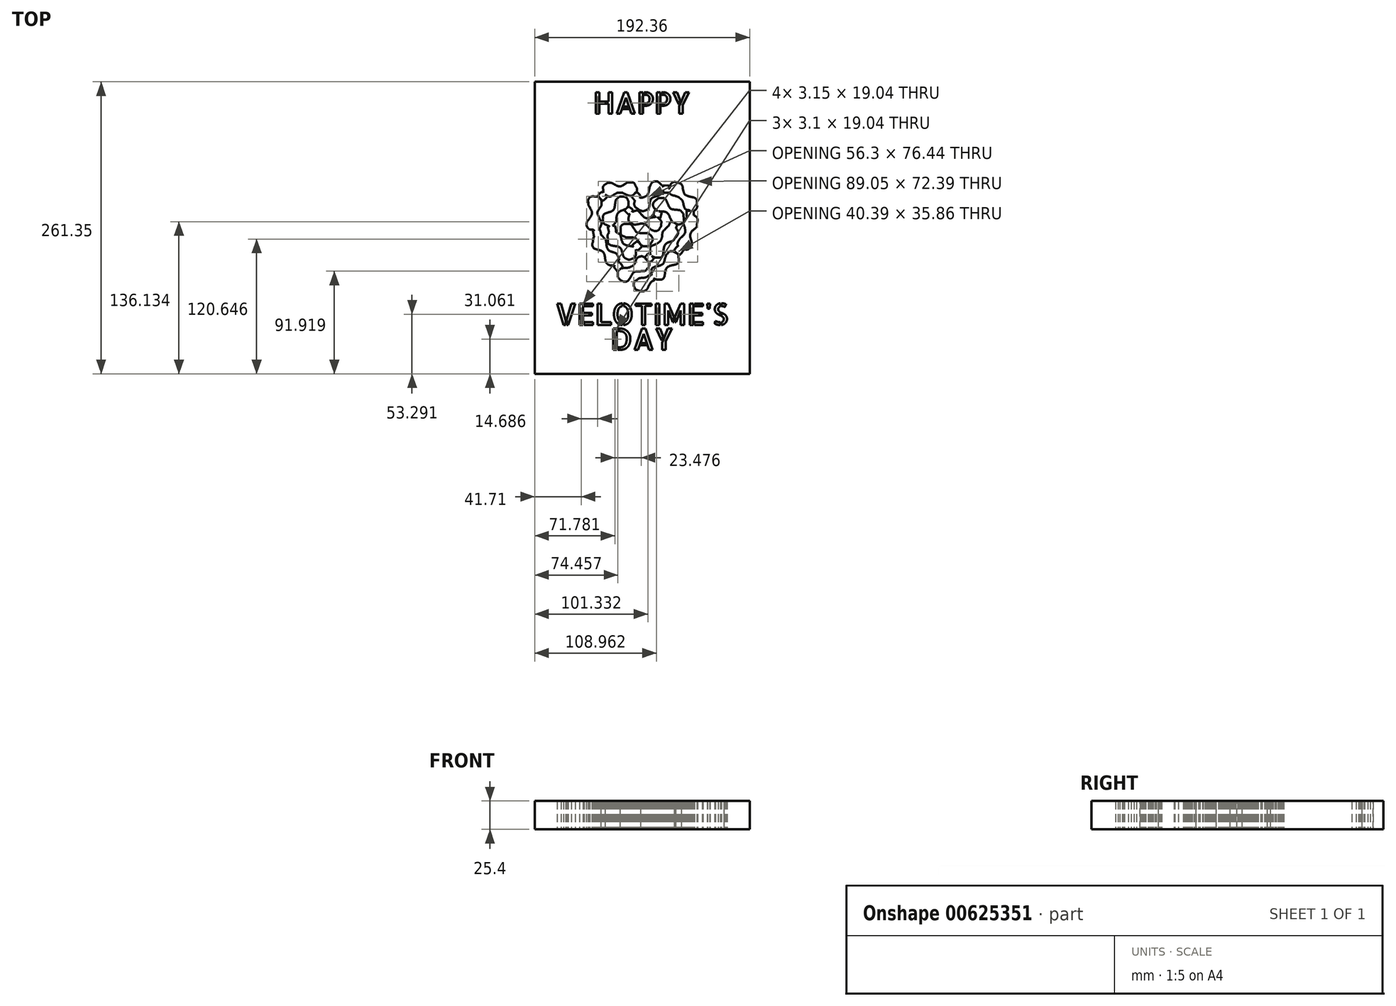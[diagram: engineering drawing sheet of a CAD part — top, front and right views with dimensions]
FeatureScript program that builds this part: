
annotation { "Feature Type Name" : "Feature", "Feature Type Description" : "" }
export const myFeature = defineFeature(function(context is Context, id is Id, definition is map)
    precondition{}
    {
        {
            var Q0;
            Q0=qCreatedBy(makeId("Top.planeOp"),FACE);
            var sketch = newSketch(context, id + "F0", { "sketchPlane" : qUnion([Q0])});
            skLineSegment(sketch, "E0", {"start": v(-21.62, 18.36) * mm, "end": v(-20.57, 16.33) * mm});
            skLineSegment(sketch, "E1", {"start": v(-20.57, 16.33) * mm, "end": v(-21.04, 14.87) * mm});
            skLineSegment(sketch, "E2", {"start": v(4.38, 19.7) * mm, "end": v(6.2, 21.31) * mm});
            skLineSegment(sketch, "E3", {"start": v(6.2, 21.31) * mm, "end": v(8.21, 19.14) * mm});
            skLineSegment(sketch, "E4", {"start": v(-25.38, 45.95) * mm, "end": v(-24.45, 45.98) * mm});
            skLineSegment(sketch, "E5", {"start": v(-24.45, 45.98) * mm, "end": v(-23.8, 43.65) * mm});
            skLineSegment(sketch, "E6", {"start": v(39.8, 56.85) * mm, "end": v(39.8, 59.27) * mm});
            skLineSegment(sketch, "E7", {"start": v(39.8, 59.27) * mm, "end": v(43.02, 59.2) * mm});
            skLineSegment(sketch, "E8", {"start": v(43.02, 59.2) * mm, "end": v(46.24, 59.12) * mm});
            skLineSegment(sketch, "E9", {"start": v(46.24, 59.12) * mm, "end": v(46.24, 56.66) * mm});
            skLineSegment(sketch, "E10", {"start": v(46.24, 56.66) * mm, "end": v(46.24, 54.2) * mm});
            skLineSegment(sketch, "E11", {"start": v(46.24, 54.2) * mm, "end": v(43.21, 54.11) * mm});
            skLineSegment(sketch, "E12", {"start": v(18.73, 78.7) * mm, "end": v(18.73, 82) * mm});
            skLineSegment(sketch, "E13", {"start": v(18.73, 82) * mm, "end": v(21.4, 81.92) * mm});
            skLineSegment(sketch, "E14", {"start": v(21.4, 81.92) * mm, "end": v(24.07, 81.84) * mm});
            skLineSegment(sketch, "E15", {"start": v(24.07, 81.84) * mm, "end": v(24.07, 78.7) * mm});
            skLineSegment(sketch, "E16", {"start": v(24.07, 78.7) * mm, "end": v(24.07, 75.54) * mm});
            skLineSegment(sketch, "E17", {"start": v(24.07, 75.54) * mm, "end": v(21.4, 75.47) * mm});
            skLineSegment(sketch, "E18", {"start": v(21.4, 75.47) * mm, "end": v(18.73, 75.39) * mm});
            skLineSegment(sketch, "E19", {"start": v(18.73, 75.39) * mm, "end": v(18.73, 78.7) * mm});
            skFitSpline(sketch, "E20", {"points": [v(-2.76, -12.29) * mm, v(-6.45, -10.34) * mm, v(-7.21, -5.2) * mm, v(-4.22, -2.42) * mm]});
            skFitSpline(sketch, "E21", {"points": [v(-4.22, -2.42) * mm, v(-3.3, -1.57) * mm, v(-1.94, -1.07) * mm, v(0.08, -0.85) * mm]});
            skFitSpline(sketch, "E22", {"points": [v(0.08, -0.85) * mm, v(2.4, -0.6) * mm, v(4.6, 0.26) * mm, v(5.86, 1.4) * mm]});
            skFitSpline(sketch, "E23", {"points": [v(5.86, 1.4) * mm, v(6.43, 1.9) * mm, v(7.02, 2.32) * mm, v(7.18, 2.32) * mm]});
            skFitSpline(sketch, "E24", {"points": [v(7.18, 2.32) * mm, v(7.56, 2.32) * mm, v(10.79, -2.16) * mm, v(10.79, -2.69) * mm]});
            skFitSpline(sketch, "E25", {"points": [v(10.79, -2.69) * mm, v(10.79, -2.91) * mm, v(10.42, -3.25) * mm, v(9.96, -3.44) * mm]});
            skFitSpline(sketch, "E26", {"points": [v(9.96, -3.44) * mm, v(8.68, -3.96) * mm, v(6.82, -6.24) * mm, v(5.54, -8.83) * mm]});
            skFitSpline(sketch, "E27", {"points": [v(5.54, -8.83) * mm, v(4.59, -10.77) * mm, v(4.17, -11.31) * mm, v(3.15, -11.96) * mm]});
            skFitSpline(sketch, "E28", {"points": [v(3.15, -11.96) * mm, v(2.1, -12.63) * mm, v(1.66, -12.74) * mm, v(0, -12.73) * mm]});
            skFitSpline(sketch, "E29", {"points": [v(0, -12.73) * mm, v(-1.22, -12.72) * mm, v(-2.25, -12.56) * mm, v(-2.76, -12.29) * mm]});
            skFitSpline(sketch, "E30", {"points": [v(-18.8, -3.07) * mm, v(-19.54, -2.69) * mm, v(-20.35, -1.94) * mm, v(-20.9, -1.13) * mm]});
            skFitSpline(sketch, "E31", {"points": [v(-20.9, -1.13) * mm, v(-21.68, 0.03) * mm, v(-21.79, 0.4) * mm, v(-21.79, 2.03) * mm]});
            skFitSpline(sketch, "E32", {"points": [v(-21.79, 2.03) * mm, v(-21.79, 4.3) * mm, v(-21.02, 5.93) * mm, v(-19.4, 7.07) * mm]});
            skFitSpline(sketch, "E33", {"points": [v(-19.4, 7.07) * mm, v(-18.4, 7.77) * mm, v(-17.97, 7.87) * mm, v(-15.04, 8.09) * mm]});
            skFitSpline(sketch, "E34", {"points": [v(-15.04, 8.09) * mm, v(-12.26, 8.3) * mm, v(-11.55, 8.45) * mm, v(-10.1, 9.17) * mm]});
            skFitSpline(sketch, "E35", {"points": [v(-10.1, 9.17) * mm, v(-8.3, 10.05) * mm, v(-6.97, 11.42) * mm, v(-5.96, 13.42) * mm]});
            skFitSpline(sketch, "E36", {"points": [v(-5.96, 13.42) * mm, v(-4, 17.32) * mm, v(0.8, 18.23) * mm, v(3.79, 15.28) * mm]});
            skFitSpline(sketch, "E37", {"points": [v(3.79, 15.28) * mm, v(6, 13.08) * mm, v(6.16, 9.55) * mm, v(4.16, 7.12) * mm]});
            skFitSpline(sketch, "E38", {"points": [v(4.16, 7.12) * mm, v(2.91, 5.6) * mm, v(1.99, 5.26) * mm, v(-1.4, 5.05) * mm]});
            skFitSpline(sketch, "E39", {"points": [v(-1.4, 5.05) * mm, v(-6.03, 4.77) * mm, v(-8.05, 3.6) * mm, v(-10.21, -0.01) * mm]});
            skFitSpline(sketch, "E40", {"points": [v(-10.21, -0.01) * mm, v(-10.75, -0.91) * mm, v(-11.4, -1.88) * mm, v(-11.63, -2.16) * mm]});
            skFitSpline(sketch, "E41", {"points": [v(-11.63, -2.16) * mm, v(-13.03, -3.79) * mm, v(-16.58, -4.24) * mm, v(-18.8, -3.07) * mm]});
            skFitSpline(sketch, "E42", {"points": [v(12.17, -2.03) * mm, v(9.83, -1.1) * mm, v(8.48, 0.99) * mm, v(8.48, 3.68) * mm]});
            skFitSpline(sketch, "E43", {"points": [v(8.48, 3.68) * mm, v(8.48, 6.78) * mm, v(9.84, 8.42) * mm, v(13.35, 9.53) * mm]});
            skFitSpline(sketch, "E44", {"points": [v(13.35, 9.53) * mm, v(17.5, 10.86) * mm, v(19.25, 12.5) * mm, v(20.39, 16.18) * mm]});
            skFitSpline(sketch, "E45", {"points": [v(20.39, 16.18) * mm, v(21.29, 19.07) * mm, v(21.73, 20) * mm, v(22.66, 20.9) * mm]});
            skFitSpline(sketch, "E46", {"points": [v(22.66, 20.9) * mm, v(24.55, 22.72) * mm, v(26.99, 23.05) * mm, v(29.42, 21.82) * mm]});
            skFitSpline(sketch, "E47", {"points": [v(29.42, 21.82) * mm, v(31.45, 20.8) * mm, v(32.48, 19.29) * mm, v(32.63, 17.13) * mm]});
            skFitSpline(sketch, "E48", {"points": [v(32.63, 17.13) * mm, v(32.89, 13.65) * mm, v(31.42, 11.73) * mm, v(27.66, 10.6) * mm]});
            skFitSpline(sketch, "E49", {"points": [v(27.66, 10.6) * mm, v(23.46, 9.36) * mm, v(21.28, 7.03) * mm, v(20.34, 2.74) * mm]});
            skFitSpline(sketch, "E50", {"points": [v(20.34, 2.74) * mm, v(19.65, -0.4) * mm, v(17.34, -2.35) * mm, v(14.36, -2.32) * mm]});
            skFitSpline(sketch, "E51", {"points": [v(14.36, -2.32) * mm, v(13.53, -2.31) * mm, v(12.54, -2.18) * mm, v(12.17, -2.03) * mm]});
            skFitSpline(sketch, "E52", {"points": [v(12.27, 1.29) * mm, v(10.96, 2.49) * mm, v(10.74, 3.96) * mm, v(11.66, 5.33) * mm]});
            skFitSpline(sketch, "E53", {"points": [v(11.66, 5.33) * mm, v(13.54, 8.1) * mm, v(17.5, 6.85) * mm, v(17.5, 3.47) * mm]});
            skFitSpline(sketch, "E54", {"points": [v(17.5, 3.47) * mm, v(17.5, 2.44) * mm, v(17.36, 2.15) * mm, v(16.47, 1.34) * mm]});
            skFitSpline(sketch, "E55", {"points": [v(16.47, 1.34) * mm, v(15.06, 0.05) * mm, v(13.65, 0.03) * mm, v(12.27, 1.29) * mm]});
            skFitSpline(sketch, "E56", {"points": [v(25.3, 13.77) * mm, v(24.73, 14.06) * mm, v(24.12, 14.7) * mm, v(23.82, 15.32) * mm]});
            skFitSpline(sketch, "E57", {"points": [v(23.82, 15.32) * mm, v(23.34, 16.27) * mm, v(23.33, 16.47) * mm, v(23.68, 17.48) * mm]});
            skFitSpline(sketch, "E58", {"points": [v(23.68, 17.48) * mm, v(24.38, 19.47) * mm, v(26.6, 20.4) * mm, v(28.3, 19.39) * mm]});
            skFitSpline(sketch, "E59", {"points": [v(28.3, 19.39) * mm, v(30.6, 18.03) * mm, v(30.45, 14.92) * mm, v(28.03, 13.67) * mm]});
            skFitSpline(sketch, "E60", {"points": [v(28.03, 13.67) * mm, v(27, 13.14) * mm, v(26.45, 13.16) * mm, v(25.3, 13.77) * mm]});
            skFitSpline(sketch, "E61", {"points": [v(-23.93, 7.17) * mm, v(-24.7, 8.22) * mm, v(-25.22, 9.16) * mm, v(-25.11, 9.35) * mm]});
            skFitSpline(sketch, "E62", {"points": [v(-25.11, 9.35) * mm, v(-24.79, 9.93) * mm, v(-21.01, 13) * mm, v(-20.62, 13) * mm]});
            skFitSpline(sketch, "E63", {"points": [v(-20.62, 13) * mm, v(-20.23, 13) * mm, v(-17.68, 9.7) * mm, v(-17.68, 9.2) * mm]});
            skFitSpline(sketch, "E64", {"points": [v(-17.68, 9.2) * mm, v(-17.68, 8.9) * mm, v(-22.02, 5.33) * mm, v(-22.37, 5.33) * mm]});
            skFitSpline(sketch, "E65", {"points": [v(-22.37, 5.33) * mm, v(-22.47, 5.33) * mm, v(-23.17, 6.16) * mm, v(-23.93, 7.17) * mm]});
            skFitSpline(sketch, "E66", {"points": [v(-29.45, 10.7) * mm, v(-30.6, 11.19) * mm, v(-31.82, 12.3) * mm, v(-32.36, 13.33) * mm]});
            skFitSpline(sketch, "E67", {"points": [v(-32.36, 13.33) * mm, v(-32.57, 13.74) * mm, v(-32.92, 15.08) * mm, v(-33.14, 16.3) * mm]});
            skFitSpline(sketch, "E68", {"points": [v(-33.14, 16.3) * mm, v(-33.88, 20.58) * mm, v(-35.68, 22.88) * mm, v(-39.36, 24.26) * mm]});
            skFitSpline(sketch, "E69", {"points": [v(-39.36, 24.26) * mm, v(-42.91, 25.58) * mm, v(-44.63, 28.37) * mm, v(-43.93, 31.64) * mm]});
            skFitSpline(sketch, "E70", {"points": [v(-43.93, 31.64) * mm, v(-43.01, 35.9) * mm, v(-37.5, 37.72) * mm, v(-34.22, 34.84) * mm]});
            skFitSpline(sketch, "E71", {"points": [v(-34.22, 34.84) * mm, v(-32.92, 33.7) * mm, v(-32.52, 32.84) * mm, v(-32.06, 30.2) * mm]});
            skFitSpline(sketch, "E72", {"points": [v(-32.06, 30.2) * mm, v(-31.33, 25.98) * mm, v(-29.5, 23.59) * mm, v(-25.96, 22.17) * mm]});
            skFitSpline(sketch, "E73", {"points": [v(-25.96, 22.17) * mm, v(-23.35, 21.12) * mm, v(-22.79, 20.63) * mm, v(-21.62, 18.36) * mm]});
            skFitSpline(sketch, "E74", {"points": [v(-21.04, 14.87) * mm, v(-21.95, 11.97) * mm, v(-24.19, 10.25) * mm, v(-27, 10.27) * mm]});
            skFitSpline(sketch, "E75", {"points": [v(-27, 10.27) * mm, v(-27.82, 10.27) * mm, v(-28.92, 10.46) * mm, v(-29.45, 10.7) * mm]});
            skFitSpline(sketch, "E76", {"points": [v(4.36, 15.2) * mm, v(3.45, 16.27) * mm, v(2.68, 17.36) * mm, v(2.63, 17.62) * mm]});
            skFitSpline(sketch, "E77", {"points": [v(2.63, 17.62) * mm, v(2.58, 17.93) * mm, v(3.2, 18.68) * mm, v(4.38, 19.7) * mm]});
            skFitSpline(sketch, "E78", {"points": [v(8.21, 19.14) * mm, v(9.32, 17.94) * mm, v(10.23, 16.82) * mm, v(10.23, 16.64) * mm]});
            skFitSpline(sketch, "E79", {"points": [v(10.23, 16.64) * mm, v(10.25, 16.19) * mm, v(6.95, 13.27) * mm, v(6.43, 13.27) * mm]});
            skFitSpline(sketch, "E80", {"points": [v(6.43, 13.27) * mm, v(6.2, 13.27) * mm, v(5.26, 14.15) * mm, v(4.36, 15.2) * mm]});
            skFitSpline(sketch, "E81", {"points": [v(-14.15, 16.27) * mm, v(-15.65, 17.07) * mm, v(-16.73, 18.5) * mm, v(-17.4, 20.56) * mm]});
            skFitSpline(sketch, "E82", {"points": [v(-17.4, 20.56) * mm, v(-18.8, 24.84) * mm, v(-20.89, 26.8) * mm, v(-25.07, 27.77) * mm]});
            skFitSpline(sketch, "E83", {"points": [v(-25.07, 27.77) * mm, v(-28.83, 28.64) * mm, v(-30.6, 30.58) * mm, v(-30.58, 33.8) * mm]});
            skFitSpline(sketch, "E84", {"points": [v(-30.58, 33.8) * mm, v(-30.56, 38.4) * mm, v(-26, 41.19) * mm, v(-21.9, 39.14) * mm]});
            skFitSpline(sketch, "E85", {"points": [v(-21.9, 39.14) * mm, v(-20.18, 38.28) * mm, v(-19.52, 37.4) * mm, v(-18.8, 35) * mm]});
            skFitSpline(sketch, "E86", {"points": [v(-18.8, 35) * mm, v(-17.57, 30.83) * mm, v(-15.25, 28.7) * mm, v(-10.83, 27.66) * mm]});
            skFitSpline(sketch, "E87", {"points": [v(-10.83, 27.66) * mm, v(-7.23, 26.81) * mm, v(-5.64, 24.96) * mm, v(-5.64, 21.61) * mm]});
            skFitSpline(sketch, "E88", {"points": [v(-5.64, 21.61) * mm, v(-5.64, 19.17) * mm, v(-7.02, 17.09) * mm, v(-9.25, 16.16) * mm]});
            skFitSpline(sketch, "E89", {"points": [v(-9.25, 16.16) * mm, v(-10.64, 15.57) * mm, v(-12.93, 15.63) * mm, v(-14.15, 16.27) * mm]});
            skFitSpline(sketch, "E90", {"points": [v(10.38, 17.83) * mm, v(8.2, 18.98) * mm, v(7.23, 20.65) * mm, v(7.23, 23.26) * mm]});
            skFitSpline(sketch, "E91", {"points": [v(7.23, 23.26) * mm, v(7.23, 26.33) * mm, v(8.01, 27.38) * mm, v(11.48, 29) * mm]});
            skFitSpline(sketch, "E92", {"points": [v(11.48, 29) * mm, v(12.84, 29.63) * mm, v(14.41, 30.55) * mm, v(14.97, 31.04) * mm]});
            skFitSpline(sketch, "E93", {"points": [v(14.97, 31.04) * mm, v(16.33, 32.24) * mm, v(17.55, 34.84) * mm, v(17.93, 37.36) * mm]});
            skFitSpline(sketch, "E94", {"points": [v(17.93, 37.36) * mm, v(18.3, 39.8) * mm, v(18.96, 41.2) * mm, v(20.16, 42.1) * mm]});
            skFitSpline(sketch, "E95", {"points": [v(20.16, 42.1) * mm, v(25.43, 46) * mm, v(32.15, 40.5) * mm, v(29.24, 34.67) * mm]});
            skFitSpline(sketch, "E96", {"points": [v(29.24, 34.67) * mm, v(28.42, 33.02) * mm, v(27.73, 32.47) * mm, v(25.23, 31.47) * mm]});
            skFitSpline(sketch, "E97", {"points": [v(25.23, 31.47) * mm, v(21.67, 30.04) * mm, v(19.87, 27.65) * mm, v(19.12, 23.38) * mm]});
            skFitSpline(sketch, "E98", {"points": [v(19.12, 23.38) * mm, v(18.38, 19.12) * mm, v(16.61, 17.36) * mm, v(13.1, 17.38) * mm]});
            skFitSpline(sketch, "E99", {"points": [v(13.1, 17.38) * mm, v(11.92, 17.4) * mm, v(10.9, 17.56) * mm, v(10.38, 17.83) * mm]});
            skFitSpline(sketch, "E100", {"points": [v(10.85, 20.91) * mm, v(9.86, 21.9) * mm, v(9.58, 23.13) * mm, v(10.08, 24.32) * mm]});
            skFitSpline(sketch, "E101", {"points": [v(10.08, 24.32) * mm, v(11.5, 27.74) * mm, v(16.26, 26.7) * mm, v(16.26, 22.97) * mm]});
            skFitSpline(sketch, "E102", {"points": [v(16.26, 22.97) * mm, v(16.26, 22.2) * mm, v(16.05, 21.76) * mm, v(15.33, 21.04) * mm]});
            skFitSpline(sketch, "E103", {"points": [v(15.33, 21.04) * mm, v(14.52, 20.23) * mm, v(14.23, 20.1) * mm, v(13.03, 20.1) * mm]});
            skFitSpline(sketch, "E104", {"points": [v(13.03, 20.1) * mm, v(11.87, 20.1) * mm, v(11.53, 20.24) * mm, v(10.85, 20.91) * mm]});
            skFitSpline(sketch, "E105", {"points": [v(22.84, 34.38) * mm, v(20.44, 35.33) * mm, v(20.07, 38.4) * mm, v(22.15, 40.05) * mm]});
            skFitSpline(sketch, "E106", {"points": [v(22.15, 40.05) * mm, v(24.11, 41.59) * mm, v(27.22, 39.99) * mm, v(27.21, 37.44) * mm]});
            skFitSpline(sketch, "E107", {"points": [v(27.21, 37.44) * mm, v(27.21, 36.32) * mm, v(26.25, 34.92) * mm, v(25.16, 34.47) * mm]});
            skFitSpline(sketch, "E108", {"points": [v(25.16, 34.47) * mm, v(24.08, 34.01) * mm, v(23.78, 34) * mm, v(22.84, 34.38) * mm]});
            skFitSpline(sketch, "E109", {"points": [v(30.92, 21.36) * mm, v(29.78, 22.35) * mm, v(28.86, 23.34) * mm, v(28.86, 23.56) * mm]});
            skFitSpline(sketch, "E110", {"points": [v(28.86, 23.56) * mm, v(28.86, 24.02) * mm, v(31.53, 27.5) * mm, v(31.9, 27.5) * mm]});
            skFitSpline(sketch, "E111", {"points": [v(31.9, 27.5) * mm, v(32.2, 27.5) * mm, v(36.52, 23.71) * mm, v(36.52, 23.44) * mm]});
            skFitSpline(sketch, "E112", {"points": [v(36.52, 23.44) * mm, v(36.52, 23.12) * mm, v(33.5, 19.56) * mm, v(33.23, 19.56) * mm]});
            skFitSpline(sketch, "E113", {"points": [v(33.23, 19.56) * mm, v(33.1, 19.56) * mm, v(32.05, 20.37) * mm, v(30.92, 21.36) * mm]});
            skFitSpline(sketch, "E114", {"points": [v(-6.7, 25.83) * mm, v(-7.77, 27.01) * mm, v(-8.65, 28.12) * mm, v(-8.65, 28.28) * mm]});
            skFitSpline(sketch, "E115", {"points": [v(-8.65, 28.28) * mm, v(-8.65, 28.62) * mm, v(-4.79, 31.6) * mm, v(-4.35, 31.6) * mm]});
            skFitSpline(sketch, "E116", {"points": [v(-4.35, 31.6) * mm, v(-3.98, 31.6) * mm, v(-0.36, 27.3) * mm, v(-0.48, 26.98) * mm]});
            skFitSpline(sketch, "E117", {"points": [v(-0.48, 26.98) * mm, v(-0.6, 26.65) * mm, v(-4.25, 23.67) * mm, v(-4.53, 23.67) * mm]});
            skFitSpline(sketch, "E118", {"points": [v(-4.53, 23.67) * mm, v(-4.66, 23.67) * mm, v(-5.63, 24.64) * mm, v(-6.7, 25.83) * mm]});
            skFitSpline(sketch, "E119", {"points": [v(36.26, 24.8) * mm, v(33.3, 25.98) * mm, v(31.64, 29.76) * mm, v(32.84, 32.63) * mm]});
            skFitSpline(sketch, "E120", {"points": [v(32.84, 32.63) * mm, v(33.07, 33.18) * mm, v(34, 34.4) * mm, v(34.9, 35.34) * mm]});
            skFitSpline(sketch, "E121", {"points": [v(34.9, 35.34) * mm, v(37.9, 38.48) * mm, v(38.65, 41.49) * mm, v(37.52, 45.9) * mm]});
            skFitSpline(sketch, "E122", {"points": [v(37.52, 45.9) * mm, v(36.8, 48.74) * mm, v(37.25, 50.43) * mm, v(39.22, 52.2) * mm]});
            skFitSpline(sketch, "E123", {"points": [v(39.22, 52.2) * mm, v(43.12, 55.73) * mm, v(49.11, 52.97) * mm, v(49.11, 47.66) * mm]});
            skFitSpline(sketch, "E124", {"points": [v(49.11, 47.66) * mm, v(49.11, 45.7) * mm, v(48.52, 44.5) * mm, v(46.62, 42.7) * mm]});
            skFitSpline(sketch, "E125", {"points": [v(46.62, 42.7) * mm, v(43.82, 40.03) * mm, v(42.98, 36.65) * mm, v(44.06, 32.37) * mm]});
            skFitSpline(sketch, "E126", {"points": [v(44.06, 32.37) * mm, v(44.66, 29.98) * mm, v(44.44, 28.42) * mm, v(43.28, 26.9) * mm]});
            skFitSpline(sketch, "E127", {"points": [v(43.28, 26.9) * mm, v(42.07, 25.32) * mm, v(40.4, 24.49) * mm, v(38.46, 24.5) * mm]});
            skFitSpline(sketch, "E128", {"points": [v(38.46, 24.5) * mm, v(37.62, 24.52) * mm, v(36.63, 24.65) * mm, v(36.26, 24.8) * mm]});
            skFitSpline(sketch, "E129", {"points": [v(-0.01, 28.1) * mm, v(-0.6, 28.45) * mm, v(-1.5, 29.29) * mm, v(-2, 29.97) * mm]});
            skFitSpline(sketch, "E130", {"points": [v(-2, 29.97) * mm, v(-4.52, 33.41) * mm, v(-6.2, 34.76) * mm, v(-8.65, 35.32) * mm]});
            skFitSpline(sketch, "E131", {"points": [v(-8.65, 35.32) * mm, v(-9.17, 35.43) * mm, v(-10.71, 35.5) * mm, v(-12.07, 35.48) * mm]});
            skFitSpline(sketch, "E132", {"points": [v(-12.07, 35.48) * mm, v(-14.29, 35.43) * mm, v(-14.7, 35.5) * mm, v(-16.04, 36.18) * mm]});
            skFitSpline(sketch, "E133", {"points": [v(-16.04, 36.18) * mm, v(-18.14, 37.25) * mm, v(-19.2, 38.97) * mm, v(-19.17, 41.3) * mm]});
            skFitSpline(sketch, "E134", {"points": [v(-19.17, 41.3) * mm, v(-19.15, 44.86) * mm, v(-16.71, 47.3) * mm, v(-13.16, 47.31) * mm]});
            skFitSpline(sketch, "E135", {"points": [v(-13.16, 47.31) * mm, v(-10.75, 47.33) * mm, v(-9.53, 46.6) * mm, v(-7.85, 44.1) * mm]});
            skFitSpline(sketch, "E136", {"points": [v(-7.85, 44.1) * mm, v(-5.3, 40.3) * mm, v(-3.82, 39.54) * mm, v(1.35, 39.28) * mm]});
            skFitSpline(sketch, "E137", {"points": [v(1.35, 39.28) * mm, v(5.09, 39.1) * mm, v(6, 38.83) * mm, v(7.13, 37.59) * mm]});
            skFitSpline(sketch, "E138", {"points": [v(7.13, 37.59) * mm, v(8.9, 35.63) * mm, v(9.25, 32.63) * mm, v(7.95, 30.41) * mm]});
            skFitSpline(sketch, "E139", {"points": [v(7.95, 30.41) * mm, v(6.82, 28.49) * mm, v(5.4, 27.66) * mm, v(3.01, 27.56) * mm]});
            skFitSpline(sketch, "E140", {"points": [v(3.01, 27.56) * mm, v(1.4, 27.5) * mm, v(0.9, 27.58) * mm, v(-0.01, 28.1) * mm]});
            skFitSpline(sketch, "E141", {"points": [v(-42.96, 35.92) * mm, v(-43.03, 36.03) * mm, v(-43.3, 37.21) * mm, v(-43.57, 38.55) * mm]});
            skFitSpline(sketch, "E142", {"points": [v(-43.57, 38.55) * mm, v(-43.94, 40.43) * mm, v(-43.97, 41.01) * mm, v(-43.71, 41.17) * mm]});
            skFitSpline(sketch, "E143", {"points": [v(-43.71, 41.17) * mm, v(-43.14, 41.53) * mm, v(-38.24, 42.68) * mm, v(-38.06, 42.5) * mm]});
            skFitSpline(sketch, "E144", {"points": [v(-38.06, 42.5) * mm, v(-37.83, 42.27) * mm, v(-36.85, 38.44) * mm, v(-36.85, 37.74) * mm]});
            skFitSpline(sketch, "E145", {"points": [v(-36.85, 37.74) * mm, v(-36.84, 37.24) * mm, v(-37.2, 37.07) * mm, v(-39.65, 36.44) * mm]});
            skFitSpline(sketch, "E146", {"points": [v(-39.65, 36.44) * mm, v(-42.75, 35.63) * mm, v(-42.78, 35.63) * mm, v(-42.96, 35.92) * mm]});
            skFitSpline(sketch, "E147", {"points": [v(-29.26, 39.47) * mm, v(-29.52, 39.9) * mm, v(-30.55, 43.84) * mm, v(-30.55, 44.4) * mm]});
            skFitSpline(sketch, "E148", {"points": [v(-30.55, 44.4) * mm, v(-30.55, 44.9) * mm, v(-30.25, 45.05) * mm, v(-28.42, 45.46) * mm]});
            skFitSpline(sketch, "E149", {"points": [v(-28.42, 45.46) * mm, v(-27.26, 45.72) * mm, v(-25.89, 45.94) * mm, v(-25.38, 45.95) * mm]});
            skFitSpline(sketch, "E150", {"points": [v(-23.8, 43.65) * mm, v(-23.45, 42.37) * mm, v(-23.21, 41.19) * mm, v(-23.27, 41.02) * mm]});
            skFitSpline(sketch, "E151", {"points": [v(-23.27, 41.02) * mm, v(-23.33, 40.86) * mm, v(-24.47, 40.45) * mm, v(-25.8, 40.12) * mm]});
            skFitSpline(sketch, "E152", {"points": [v(-25.8, 40.12) * mm, v(-27.13, 39.8) * mm, v(-28.42, 39.46) * mm, v(-28.68, 39.39) * mm]});
            skFitSpline(sketch, "E153", {"points": [v(-28.68, 39.39) * mm, v(-28.93, 39.31) * mm, v(-29.19, 39.35) * mm, v(-29.26, 39.47) * mm]});
            skFitSpline(sketch, "E154", {"points": [v(9.2, 41.78) * mm, v(8.63, 41.94) * mm, v(7.49, 42.83) * mm, v(6.22, 44.1) * mm]});
            skFitSpline(sketch, "E155", {"points": [v(6.22, 44.1) * mm, v(4.14, 46.2) * mm, v(2.21, 47.36) * mm, v(0.27, 47.67) * mm]});
            skFitSpline(sketch, "E156", {"points": [v(0.27, 47.67) * mm, v(-0.26, 47.76) * mm, v(-1.81, 47.61) * mm, v(-3.17, 47.35) * mm]});
            skFitSpline(sketch, "E157", {"points": [v(-3.17, 47.35) * mm, v(-6.08, 46.78) * mm, v(-7.38, 46.9) * mm, v(-9.05, 47.88) * mm]});
            skFitSpline(sketch, "E158", {"points": [v(-9.05, 47.88) * mm, v(-11.24, 49.16) * mm, v(-12.35, 52.02) * mm, v(-11.66, 54.6) * mm]});
            skFitSpline(sketch, "E159", {"points": [v(-11.66, 54.6) * mm, v(-11.23, 56.2) * mm, v(-9.22, 58.25) * mm, v(-7.69, 58.68) * mm]});
            skFitSpline(sketch, "E160", {"points": [v(-7.69, 58.68) * mm, v(-4.98, 59.42) * mm, v(-3.3, 58.87) * mm, v(-1.03, 56.49) * mm]});
            skFitSpline(sketch, "E161", {"points": [v(-1.03, 56.49) * mm, v(1.85, 53.45) * mm, v(4.52, 52.4) * mm, v(7.8, 52.97) * mm]});
            skFitSpline(sketch, "E162", {"points": [v(7.8, 52.97) * mm, v(12.18, 53.74) * mm, v(13.33, 53.6) * mm, v(15.07, 52.07) * mm]});
            skFitSpline(sketch, "E163", {"points": [v(15.07, 52.07) * mm, v(16.62, 50.71) * mm, v(17.16, 49.36) * mm, v(17.04, 47.18) * mm]});
            skFitSpline(sketch, "E164", {"points": [v(17.04, 47.18) * mm, v(16.95, 45.66) * mm, v(16.78, 45.1) * mm, v(16.12, 44.14) * mm]});
            skFitSpline(sketch, "E165", {"points": [v(16.12, 44.14) * mm, v(14.63, 42) * mm, v(11.79, 41.03) * mm, v(9.2, 41.78) * mm]});
            skFitSpline(sketch, "E166", {"points": [v(-44.14, 42.26) * mm, v(-48.28, 43.3) * mm, v(-49.83, 47.83) * mm, v(-47.43, 51.86) * mm]});
            skFitSpline(sketch, "E167", {"points": [v(-47.43, 51.86) * mm, v(-45.13, 55.72) * mm, v(-45.01, 58.39) * mm, v(-46.97, 62.27) * mm]});
            skFitSpline(sketch, "E168", {"points": [v(-46.97, 62.27) * mm, v(-47.95, 64.2) * mm, v(-48.15, 64.85) * mm, v(-48.14, 66.12) * mm]});
            skFitSpline(sketch, "E169", {"points": [v(-48.14, 66.12) * mm, v(-48.11, 69.54) * mm, v(-45.68, 71.92) * mm, v(-42.18, 71.96) * mm]});
            skFitSpline(sketch, "E170", {"points": [v(-42.18, 71.96) * mm, v(-40.12, 71.98) * mm, v(-38.46, 71.13) * mm, v(-37.27, 69.43) * mm]});
            skFitSpline(sketch, "E171", {"points": [v(-37.27, 69.43) * mm, v(-36.51, 68.35) * mm, v(-36.43, 68.04) * mm, v(-36.43, 66.12) * mm]});
            skFitSpline(sketch, "E172", {"points": [v(-36.43, 66.12) * mm, v(-36.43, 64.15) * mm, v(-36.5, 63.89) * mm, v(-37.46, 62.33) * mm]});
            skFitSpline(sketch, "E173", {"points": [v(-37.46, 62.33) * mm, v(-39.83, 58.5) * mm, v(-39.92, 56.52) * mm, v(-37.94, 51.98) * mm]});
            skFitSpline(sketch, "E174", {"points": [v(-37.94, 51.98) * mm, v(-36.5, 48.65) * mm, v(-36.32, 47.6) * mm, v(-36.97, 46.05) * mm]});
            skFitSpline(sketch, "E175", {"points": [v(-36.97, 46.05) * mm, v(-38.14, 43.23) * mm, v(-41.32, 41.56) * mm, v(-44.14, 42.26) * mm]});
            skFitSpline(sketch, "E176", {"points": [v(26.4, 43.27) * mm, v(25.11, 43.8) * mm, v(23.96, 44.34) * mm, v(23.84, 44.46) * mm]});
            skFitSpline(sketch, "E177", {"points": [v(23.84, 44.46) * mm, v(23.59, 44.7) * mm, v(25.5, 49.4) * mm, v(25.86, 49.4) * mm]});
            skFitSpline(sketch, "E178", {"points": [v(25.86, 49.4) * mm, v(26.3, 49.4) * mm, v(31.32, 46.96) * mm, v(31.32, 46.75) * mm]});
            skFitSpline(sketch, "E179", {"points": [v(31.32, 46.75) * mm, v(31.32, 46.63) * mm, v(30.94, 45.57) * mm, v(30.47, 44.4) * mm]});
            skFitSpline(sketch, "E180", {"points": [v(30.47, 44.4) * mm, v(29.89, 42.95) * mm, v(29.48, 42.29) * mm, v(29.17, 42.3) * mm]});
            skFitSpline(sketch, "E181", {"points": [v(29.17, 42.3) * mm, v(28.92, 42.3) * mm, v(27.67, 42.74) * mm, v(26.4, 43.27) * mm]});
            skFitSpline(sketch, "E182", {"points": [v(-31.5, 46.36) * mm, v(-33.7, 47.38) * mm, v(-34.93, 49.4) * mm, v(-34.93, 52) * mm]});
            skFitSpline(sketch, "E183", {"points": [v(-34.93, 52) * mm, v(-34.93, 54.72) * mm, v(-33.62, 56.43) * mm, v(-30.65, 57.62) * mm]});
            skFitSpline(sketch, "E184", {"points": [v(-30.65, 57.62) * mm, v(-26.5, 59.27) * mm, v(-24.92, 61.26) * mm, v(-24.1, 65.85) * mm]});
            skFitSpline(sketch, "E185", {"points": [v(-24.1, 65.85) * mm, v(-23.65, 68.47) * mm, v(-23.22, 69.32) * mm, v(-21.75, 70.59) * mm]});
            skFitSpline(sketch, "E186", {"points": [v(-21.75, 70.59) * mm, v(-20.45, 71.7) * mm, v(-19.42, 71.97) * mm, v(-17.25, 71.79) * mm]});
            skFitSpline(sketch, "E187", {"points": [v(-17.25, 71.79) * mm, v(-15.35, 71.63) * mm, v(-13.74, 70.56) * mm, v(-12.82, 68.84) * mm]});
            skFitSpline(sketch, "E188", {"points": [v(-12.82, 68.84) * mm, v(-12.27, 67.8) * mm, v(-12.18, 67.3) * mm, v(-12.26, 65.64) * mm]});
            skFitSpline(sketch, "E189", {"points": [v(-12.26, 65.64) * mm, v(-12.34, 63.98) * mm, v(-12.48, 63.5) * mm, v(-13.17, 62.52) * mm]});
            skFitSpline(sketch, "E190", {"points": [v(-13.17, 62.52) * mm, v(-14, 61.36) * mm, v(-14.45, 61.06) * mm, v(-17.73, 59.54) * mm]});
            skFitSpline(sketch, "E191", {"points": [v(-17.73, 59.54) * mm, v(-20.84, 58.1) * mm, v(-22.54, 55.58) * mm, v(-23.01, 51.73) * mm]});
            skFitSpline(sketch, "E192", {"points": [v(-23.01, 51.73) * mm, v(-23.24, 49.85) * mm, v(-23.86, 48.49) * mm, v(-24.98, 47.43) * mm]});
            skFitSpline(sketch, "E193", {"points": [v(-24.98, 47.43) * mm, v(-26.65, 45.84) * mm, v(-29.4, 45.4) * mm, v(-31.5, 46.36) * mm]});
            skFitSpline(sketch, "E194", {"points": [v(29.03, 48.43) * mm, v(27.46, 49) * mm, v(26.48, 50.08) * mm, v(25.13, 52.76) * mm]});
            skFitSpline(sketch, "E195", {"points": [v(25.13, 52.76) * mm, v(23.18, 56.62) * mm, v(21.14, 58.12) * mm, v(17.22, 58.57) * mm]});
            skFitSpline(sketch, "E196", {"points": [v(17.22, 58.57) * mm, v(14.9, 58.83) * mm, v(13.9, 59.2) * mm, v(12.78, 60.17) * mm]});
            skFitSpline(sketch, "E197", {"points": [v(12.78, 60.17) * mm, v(10.12, 62.5) * mm, v(10.1, 66.5) * mm, v(12.75, 69.03) * mm]});
            skFitSpline(sketch, "E198", {"points": [v(12.75, 69.03) * mm, v(13.94, 70.16) * mm, v(14.84, 70.48) * mm, v(16.84, 70.48) * mm]});
            skFitSpline(sketch, "E199", {"points": [v(16.84, 70.48) * mm, v(19.73, 70.48) * mm, v(21.07, 69.46) * mm, v(22.7, 66) * mm]});
            skFitSpline(sketch, "E200", {"points": [v(22.7, 66) * mm, v(24.46, 62.26) * mm, v(26.7, 60.66) * mm, v(31.03, 60.07) * mm]});
            skFitSpline(sketch, "E201", {"points": [v(31.03, 60.07) * mm, v(33.72, 59.71) * mm, v(34.48, 59.38) * mm, v(35.68, 58) * mm]});
            skFitSpline(sketch, "E202", {"points": [v(35.68, 58) * mm, v(36.82, 56.7) * mm, v(37.07, 56) * mm, v(37.06, 54.1) * mm]});
            skFitSpline(sketch, "E203", {"points": [v(37.06, 54.1) * mm, v(37.05, 49.75) * mm, v(33.12, 46.98) * mm, v(29.03, 48.43) * mm]});
            skFitSpline(sketch, "E204", {"points": [v(13.15, 53.51) * mm, v(11.81, 53.94) * mm, v(10.6, 54.42) * mm, v(10.44, 54.57) * mm]});
            skFitSpline(sketch, "E205", {"points": [v(10.44, 54.57) * mm, v(10.13, 54.88) * mm, v(11.22, 59.15) * mm, v(11.67, 59.43) * mm]});
            skFitSpline(sketch, "E206", {"points": [v(11.67, 59.43) * mm, v(12.03, 59.65) * mm, v(17.13, 57.81) * mm, v(17.3, 57.4) * mm]});
            skFitSpline(sketch, "E207", {"points": [v(17.3, 57.4) * mm, v(17.37, 57.2) * mm, v(17.24, 56.4) * mm, v(17, 55.62) * mm]});
            skFitSpline(sketch, "E208", {"points": [v(17, 55.62) * mm, v(16.77, 54.83) * mm, v(16.5, 53.85) * mm, v(16.42, 53.44) * mm]});
            skFitSpline(sketch, "E209", {"points": [v(16.42, 53.44) * mm, v(16.22, 52.53) * mm, v(16.21, 52.53) * mm, v(13.15, 53.51) * mm]});
            skFitSpline(sketch, "E210", {"points": [v(40, 54.23) * mm, v(39.9, 54.33) * mm, v(39.8, 55.51) * mm, v(39.8, 56.85) * mm]});
            skFitSpline(sketch, "E211", {"points": [v(43.21, 54.11) * mm, v(41.55, 54.07) * mm, v(40.1, 54.12) * mm, v(40, 54.23) * mm]});
            skFitSpline(sketch, "E212", {"points": [v(-13.92, 57.55) * mm, v(-14.79, 58.42) * mm, v(-15.5, 59.28) * mm, v(-15.5, 59.45) * mm]});
            skFitSpline(sketch, "E213", {"points": [v(-15.5, 59.45) * mm, v(-15.5, 59.81) * mm, v(-12.33, 62.68) * mm, v(-11.93, 62.68) * mm]});
            skFitSpline(sketch, "E214", {"points": [v(-11.93, 62.68) * mm, v(-11.51, 62.68) * mm, v(-8.37, 59.8) * mm, v(-8.4, 59.45) * mm]});
            skFitSpline(sketch, "E215", {"points": [v(-8.4, 59.45) * mm, v(-8.43, 59.09) * mm, v(-11.78, 55.97) * mm, v(-12.14, 55.97) * mm]});
            skFitSpline(sketch, "E216", {"points": [v(-12.14, 55.97) * mm, v(-12.26, 55.97) * mm, v(-13.06, 56.68) * mm, v(-13.92, 57.55) * mm]});
            skFitSpline(sketch, "E217", {"points": [v(-0.3, 59.1) * mm, v(-0.45, 59.16) * mm, v(-0.91, 59.28) * mm, v(-1.33, 59.38) * mm]});
            skFitSpline(sketch, "E218", {"points": [v(-1.33, 59.38) * mm, v(-1.75, 59.47) * mm, v(-2.6, 60) * mm, v(-3.22, 60.56) * mm]});
            skFitSpline(sketch, "E219", {"points": [v(-3.22, 60.56) * mm, v(-6.85, 63.84) * mm, v(-5.65, 69.48) * mm, v(-1.03, 70.85) * mm]});
            skFitSpline(sketch, "E220", {"points": [v(-1.03, 70.85) * mm, v(3.28, 72.13) * mm, v(5.3, 74.33) * mm, v(6.37, 78.92) * mm]});
            skFitSpline(sketch, "E221", {"points": [v(6.37, 78.92) * mm, v(6.65, 80.16) * mm, v(7.2, 81.64) * mm, v(7.59, 82.22) * mm]});
            skFitSpline(sketch, "E222", {"points": [v(7.59, 82.22) * mm, v(9.38, 84.93) * mm, v(13.93, 85.3) * mm, v(16.5, 82.97) * mm]});
            skFitSpline(sketch, "E223", {"points": [v(16.5, 82.97) * mm, v(18.41, 81.23) * mm, v(18.9, 77.91) * mm, v(17.58, 75.66) * mm]});
            skFitSpline(sketch, "E224", {"points": [v(17.58, 75.66) * mm, v(16.7, 74.16) * mm, v(15.44, 73.27) * mm, v(12.74, 72.24) * mm]});
            skFitSpline(sketch, "E225", {"points": [v(12.74, 72.24) * mm, v(9.18, 70.87) * mm, v(7.36, 68.65) * mm, v(6.65, 64.8) * mm]});
            skFitSpline(sketch, "E226", {"points": [v(6.65, 64.8) * mm, v(6.17, 62.2) * mm, v(5.15, 60.68) * mm, v(3.26, 59.73) * mm]});
            skFitSpline(sketch, "E227", {"points": [v(3.26, 59.73) * mm, v(2.42, 59.3) * mm, v(0.2, 58.92) * mm, v(-0.3, 59.1) * mm]});
            skFitSpline(sketch, "E228", {"points": [v(41.59, 59.83) * mm, v(39.15, 60.42) * mm, v(37.76, 62.04) * mm, v(36.94, 65.28) * mm]});
            skFitSpline(sketch, "E229", {"points": [v(36.94, 65.28) * mm, v(36.36, 67.52) * mm, v(35.47, 69.07) * mm, v(34.04, 70.3) * mm]});
            skFitSpline(sketch, "E230", {"points": [v(34.04, 70.3) * mm, v(32.98, 71.2) * mm, v(32.03, 71.65) * mm, v(28.72, 72.82) * mm]});
            skFitSpline(sketch, "E231", {"points": [v(28.72, 72.82) * mm, v(25.44, 73.98) * mm, v(23.76, 77.29) * mm, v(24.87, 80.4) * mm]});
            skFitSpline(sketch, "E232", {"points": [v(24.87, 80.4) * mm, v(26.03, 83.67) * mm, v(28.99, 85.12) * mm, v(32.5, 84.15) * mm]});
            skFitSpline(sketch, "E233", {"points": [v(32.5, 84.15) * mm, v(34.02, 83.73) * mm, v(35.85, 81.85) * mm, v(36.22, 80.33) * mm]});
            skFitSpline(sketch, "E234", {"points": [v(36.22, 80.33) * mm, v(37.48, 75.06) * mm, v(39.18, 73.11) * mm, v(43.72, 71.72) * mm]});
            skFitSpline(sketch, "E235", {"points": [v(43.72, 71.72) * mm, v(47.42, 70.58) * mm, v(48.9, 68.87) * mm, v(48.92, 65.7) * mm]});
            skFitSpline(sketch, "E236", {"points": [v(48.92, 65.7) * mm, v(48.95, 61.7) * mm, v(45.47, 58.9) * mm, v(41.59, 59.83) * mm]});
            skFitSpline(sketch, "E237", {"points": [v(40.74, 63.47) * mm, v(40.02, 64.2) * mm, v(39.8, 64.63) * mm, v(39.8, 65.4) * mm]});
            skFitSpline(sketch, "E238", {"points": [v(39.8, 65.4) * mm, v(39.8, 67.48) * mm, v(41.08, 68.84) * mm, v(43.04, 68.84) * mm]});
            skFitSpline(sketch, "E239", {"points": [v(43.04, 68.84) * mm, v(44.04, 68.84) * mm, v(44.4, 68.68) * mm, v(45.17, 67.9) * mm]});
            skFitSpline(sketch, "E240", {"points": [v(45.17, 67.9) * mm, v(45.97, 67.11) * mm, v(46.1, 66.79) * mm, v(46.1, 65.69) * mm]});
            skFitSpline(sketch, "E241", {"points": [v(46.1, 65.69) * mm, v(46.1, 64.6) * mm, v(45.97, 64.27) * mm, v(45.17, 63.47) * mm]});
            skFitSpline(sketch, "E242", {"points": [v(45.17, 63.47) * mm, v(44.38, 62.68) * mm, v(44.05, 62.54) * mm, v(42.96, 62.54) * mm]});
            skFitSpline(sketch, "E243", {"points": [v(42.96, 62.54) * mm, v(41.86, 62.54) * mm, v(41.53, 62.68) * mm, v(40.74, 63.47) * mm]});
            skFitSpline(sketch, "E244", {"points": [v(29.41, 75.5) * mm, v(28.05, 75.96) * mm, v(27.13, 77.42) * mm, v(27.31, 78.83) * mm]});
            skFitSpline(sketch, "E245", {"points": [v(27.31, 78.83) * mm, v(27.72, 81.95) * mm, v(32.01, 82.75) * mm, v(33.34, 79.96) * mm]});
            skFitSpline(sketch, "E246", {"points": [v(33.34, 79.96) * mm, v(33.88, 78.8) * mm, v(33.9, 78.39) * mm, v(33.4, 77.2) * mm]});
            skFitSpline(sketch, "E247", {"points": [v(33.4, 77.2) * mm, v(32.75, 75.64) * mm, v(31.09, 74.93) * mm, v(29.41, 75.5) * mm]});
            skFitSpline(sketch, "E248", {"points": [v(-7.78, 69.76) * mm, v(-8.56, 70.72) * mm, v(-9.19, 71.68) * mm, v(-9.18, 71.88) * mm]});
            skFitSpline(sketch, "E249", {"points": [v(-9.18, 71.88) * mm, v(-9.16, 72.28) * mm, v(-5.07, 75.68) * mm, v(-4.6, 75.68) * mm]});
            skFitSpline(sketch, "E250", {"points": [v(-4.6, 75.68) * mm, v(-4.27, 75.68) * mm, v(-1.53, 72.38) * mm, v(-1.53, 71.99) * mm]});
            skFitSpline(sketch, "E251", {"points": [v(-1.53, 71.99) * mm, v(-1.54, 71.58) * mm, v(-5.53, 68.02) * mm, v(-5.98, 68.02) * mm]});
            skFitSpline(sketch, "E252", {"points": [v(-5.98, 68.02) * mm, v(-6.19, 68.02) * mm, v(-7, 68.8) * mm, v(-7.78, 69.76) * mm]});
            skFitSpline(sketch, "E253", {"points": [v(-37.5, 70.3) * mm, v(-38.5, 71.41) * mm, v(-39.3, 72.51) * mm, v(-39.3, 72.75) * mm]});
            skFitSpline(sketch, "E254", {"points": [v(-39.3, 72.75) * mm, v(-39.3, 73.22) * mm, v(-36.37, 75.95) * mm, v(-35.86, 75.95) * mm]});
            skFitSpline(sketch, "E255", {"points": [v(-35.86, 75.95) * mm, v(-35.5, 75.95) * mm, v(-31.64, 71.98) * mm, v(-31.64, 71.6) * mm]});
            skFitSpline(sketch, "E256", {"points": [v(-31.64, 71.6) * mm, v(-31.64, 71.3) * mm, v(-35.07, 68.29) * mm, v(-35.42, 68.29) * mm]});
            skFitSpline(sketch, "E257", {"points": [v(-35.42, 68.29) * mm, v(-35.57, 68.29) * mm, v(-36.51, 69.2) * mm, v(-37.5, 70.3) * mm]});
            skFitSpline(sketch, "E258", {"points": [v(-31.98, 73.15) * mm, v(-33.93, 74.28) * mm, v(-34.76, 75.66) * mm, v(-34.87, 78) * mm]});
            skFitSpline(sketch, "E259", {"points": [v(-34.87, 78) * mm, v(-35, 80.46) * mm, v(-34.27, 81.98) * mm, v(-32.35, 83.28) * mm]});
            skFitSpline(sketch, "E260", {"points": [v(-32.35, 83.28) * mm, v(-31.19, 84.06) * mm, v(-30.81, 84.17) * mm, v(-29.2, 84.17) * mm]});
            skFitSpline(sketch, "E261", {"points": [v(-29.2, 84.17) * mm, v(-27.61, 84.17) * mm, v(-27.07, 84.02) * mm, v(-25.06, 83.03) * mm]});
            skFitSpline(sketch, "E262", {"points": [v(-25.06, 83.03) * mm, v(-21.1, 81.1) * mm, v(-18.69, 81.23) * mm, v(-14.77, 83.61) * mm]});
            skFitSpline(sketch, "E263", {"points": [v(-14.77, 83.61) * mm, v(-12.96, 84.71) * mm, v(-12.82, 84.75) * mm, v(-10.92, 84.66) * mm]});
            skFitSpline(sketch, "E264", {"points": [v(-10.92, 84.66) * mm, v(-8.39, 84.54) * mm, v(-6.95, 83.63) * mm, v(-5.84, 81.45) * mm]});
            skFitSpline(sketch, "E265", {"points": [v(-5.84, 81.45) * mm, v(-4.55, 78.9) * mm, v(-4.94, 76.55) * mm, v(-6.98, 74.57) * mm]});
            skFitSpline(sketch, "E266", {"points": [v(-6.98, 74.57) * mm, v(-8.46, 73.13) * mm, v(-10.2, 72.5) * mm, v(-11.85, 72.8) * mm]});
            skFitSpline(sketch, "E267", {"points": [v(-11.85, 72.8) * mm, v(-12.42, 72.9) * mm, v(-13.93, 73.5) * mm, v(-15.2, 74.13) * mm]});
            skFitSpline(sketch, "E268", {"points": [v(-15.2, 74.13) * mm, v(-17.38, 75.2) * mm, v(-17.67, 75.27) * mm, v(-19.86, 75.27) * mm]});
            skFitSpline(sketch, "E269", {"points": [v(-19.86, 75.27) * mm, v(-22.35, 75.27) * mm, v(-22.65, 75.17) * mm, v(-25.76, 73.36) * mm]});
            skFitSpline(sketch, "E270", {"points": [v(-25.76, 73.36) * mm, v(-27.94, 72.09) * mm, v(-30.02, 72.02) * mm, v(-31.98, 73.15) * mm]});
            skText(sketch, "E271", { "text": "HAPPY ", "fontName": "AllertaStencil-Regular.ttf"});
            skText(sketch, "E272", { "text": "VELOTIME\'S ", "fontName": "AllertaStencil-Regular.ttf"});
            skText(sketch, "E273", { "text": "DAY", "fontName": "AllertaStencil-Regular.ttf"});
            skLineSegment(sketch, "E274", {"start": v(0, -46.15) * mm, "end": v(0, -42.97) * mm, "construction": true});
            skLineSegment(sketch, "E275", {"start": v(0, 165.4) * mm, "end": v(0, 0) * mm, "construction": true});
            skLineSegment(sketch, "E276", {"start": v(0, 146.35) * mm, "end": v(0, -23.92) * mm, "construction": true});
            skArc(sketch, "E277", {"start": v(-6.35, 132.28) * mm, "mid": v(-8.2, 136.77) * mm, "end": v(-12.7, 138.63) * mm});
            skLineSegment(sketch, "E278", {"start": v(-6.35, 132.28) * mm, "end": v(-6.35, 89.68) * mm});
            skArc(sketch, "E279", {"start": v(-6.35, 89.68) * mm, "mid": v(-38.42, 90.41) * mm, "end": v(-56.15, 63.68) * mm});
            skFitSpline(sketch, "E280", {"points": [v(-56.15, 63.68) * mm, v(-41.66, 15.91) * mm, v(-12.3, -13.23) * mm], "startDerivative": vector(-5.78, -70.68) * mm, "endDerivative": vector(52.44, -33.52) * mm});
            skLineSegment(sketch, "E281", {"start": v(-12.7, 138.63) * mm, "end": v(-22.77, 138.63) * mm, "construction": true});
            skArc(sketch, "E282.MirrorCS", {"start": v(6.35, 132.28) * mm, "mid": v(8.2, 136.77) * mm, "end": v(12.7, 138.63) * mm});
            skLineSegment(sketch, "E283.MirrorCS", {"start": v(6.35, 132.28) * mm, "end": v(6.35, 89.68) * mm});
            skArc(sketch, "E284.MirrorCS", {"start": v(6.35, 89.68) * mm, "mid": v(38.42, 90.41) * mm, "end": v(56.15, 63.68) * mm});
            skFitSpline(sketch, "E285.MirrorCS", {"points": [v(56.15, 63.68) * mm, v(41.66, 15.91) * mm, v(12.3, -13.23) * mm], "startDerivative": vector(5.78, -70.68) * mm, "endDerivative": vector(-52.44, -33.52) * mm});
            skLineSegment(sketch, "E286.bottom", {"start": v(-96.18, 174.6) * mm, "end": v(96.18, 174.6) * mm});
            skLineSegment(sketch, "E286.top", {"start": v(-96.18, -86.74) * mm, "end": v(96.18, -86.74) * mm});
            skLineSegment(sketch, "E286.left", {"start": v(-96.18, 174.6) * mm, "end": v(-96.18, -86.74) * mm});
            skLineSegment(sketch, "E286.right", {"start": v(96.18, 174.6) * mm, "end": v(96.18, -86.74) * mm});
            skPoint(sketch, "E286.middle", {"position": v(0, 43.93) * mm});
            const initialGuessF0  = {"E271": [-0.04379, 0.14635, 1, 0, 0.01905], "E272": [-0.0777, -0.04297, 1, 0, 0.01905], "E273": [-0.02843, -0.0652, 1, 0, 0.01905]};
            skSetInitialGuess(sketch, initialGuessF0);
            skSolve(sketch);
        }
        {
            var Q0;
            Q0 = qSketchRegion(id + "F0", true);
            extrude(context, id + "F1", {"entities" : qUnion([Q0]), "depth" : 25.4 * mm, "offsetDistance" : 25.4 * mm});
        }
    });
